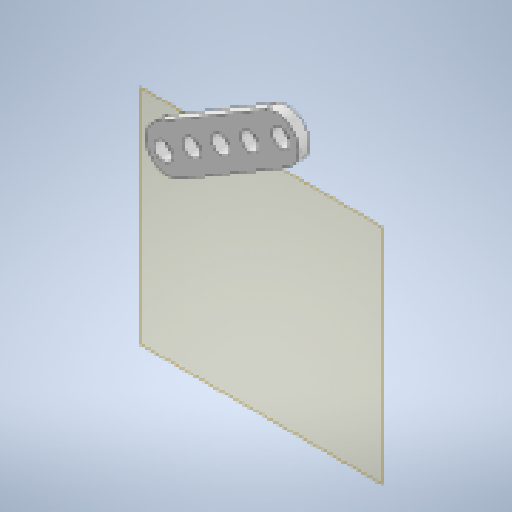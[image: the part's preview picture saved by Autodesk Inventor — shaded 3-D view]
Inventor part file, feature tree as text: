
AUTODESK INVENTOR PART (.ipt)
format: ipt  version: 2024.1 (Build 281209000, 209)  size: 166,912 bytes
history: native  units: mm
features: other x4, reference x2, plane x1, extrude x1, fillet x1, sketch x1
ambient origin geometry x8: Origin, YZ Plane, XZ Plane, XY Plane, X Axis, Y Axis, Z Axis, Center Point
bodies: Solid1 (feature_tree)
feature tree (10):
  plane  "Work Plane1"
  extrude  "Extrusion1"  Depth=8.0mm
  fillet  "Fillet1"  Radius=3.0mm
  sketch  "Sketch1"  dims[d0=4.0mm d1=8.0mm d2=3.0mm d3=3.0mm d4=4.0mm d5=40.0mm d7=6.0mm d8=10.0mm d10=10.0mm d12=2.0mm d13=0.0mm d14=4.0mm]
  reference  "Reference1"
  reference  "Reference2"
  other  "<userpath>\Documents\0004-CAD\3D-cad-main\the-artifact\artifact-assembly.iam"
  other  "artifact-assembly.iam"
  other  "control-arm:1"
  other  "leaf-lid:1"
